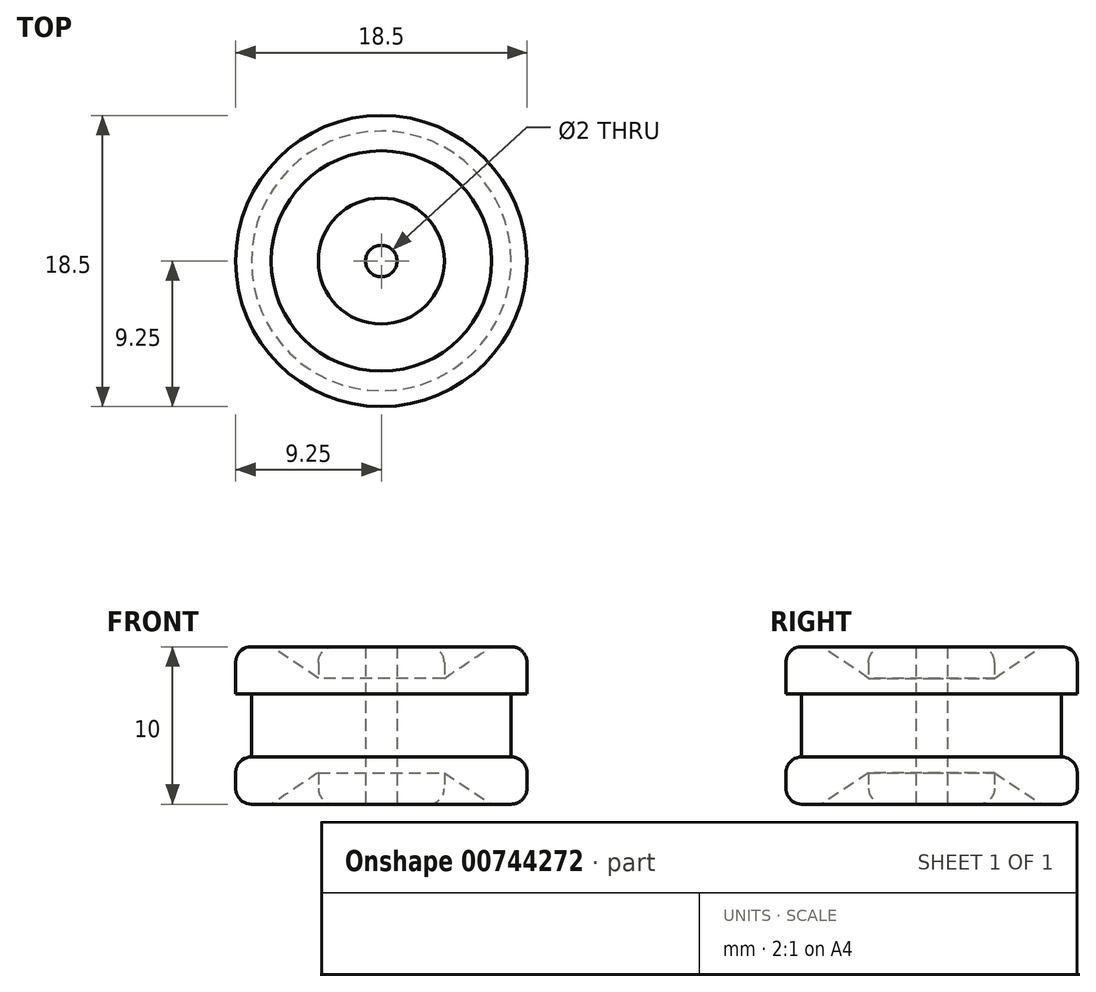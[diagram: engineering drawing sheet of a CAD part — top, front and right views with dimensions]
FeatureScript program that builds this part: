
annotation { "Feature Type Name" : "Feature", "Feature Type Description" : "" }
export const myFeature = defineFeature(function(context is Context, id is Id, definition is map)
    precondition{}
    {
        {
            var Q0;
            Q0=qCreatedBy(makeId("Top.planeOp"),FACE);
            var sketch = newSketch(context, id + "F0", { "sketchPlane" : qUnion([Q0])});
            skCircle(sketch, "E0", {"center": v(0, 0) * mm, "radius": 9.25 * mm});
            skCircle(sketch, "E1", {"center": v(0, 0) * mm, "radius": 1 * mm});
            skSolve(sketch);
        }
        {
            var Q0;
            Q0 = qSketchRegion(id + "F0", true);
            extrude(context, id + "F1", {"entities" : qUnion([Q0]), "depth" : 10 * mm, "offsetDistance" : 25 * mm});
        }
        {
            var Q0;
            Q0=makeQuery(id+"F1.opExtrude","CAP_FACE",FACE,{"disambiguationData":[OSD([sQuery(id+"F0.wireOp",EDGE,"E0"),sQuery(id+"F0.wireOp",EDGE,"E1")])],"isStart":false});
            cPlane(context, id + "F2", {"entities" : qUnion([Q0]), "cplaneType" : CPlaneType.OFFSET, "offset" : 2 * mm, "oppositeDirection" : true, "width" : 150 * mm, "height" : 150 * mm});
        }
        {
            var Q0;
            Q0=qCreatedBy(id+"F2.planeOp",FACE);
            var sketch = newSketch(context, id + "F3", { "sketchPlane" : qUnion([Q0])});
            skCircle(sketch, "E2", {"center": v(0, 0) * mm, "radius": 4 * mm});
            skSolve(sketch);
        }
        {
            var Q0;
            Q0=makeQuery(id+"F1.opExtrude","CAP_FACE",FACE,{"disambiguationData":[OSD([sQuery(id+"F0.wireOp",EDGE,"E0"),sQuery(id+"F0.wireOp",EDGE,"E1")])],"isStart":false});
            var sketch = newSketch(context, id + "F4", { "sketchPlane" : qUnion([Q0])});
            skCircle(sketch, "E3", {"center": v(0, 0) * mm, "radius": 7 * mm});
            skSolve(sketch);
        }
        {
            var Q1;
            Q1 = qSketchRegion(id + "F4", true);
            var Q2;
            Q2 = qSketchRegion(id + "F3", true);
            loft(context, id + "F5", {"operationType" : NewBodyOperationType.REMOVE, "sheetProfilesArray" : [{ "sheetProfileEntities" : qUnion([Q1]) }, { "sheetProfileEntities" : qUnion([Q2]) }]});
        }
        {
            var Q0;
            Q0=makeQuery(id+"F0.imprint","IMPRINT",FACE,{"disambiguationData":[TD([[makeQuery(id+"F0.imprint","IMPRINT",EDGE,{"derivedFrom":sQuery(id+"F0.wireOp",EDGE,"E0")}),1.0]])]});
            cPlane(context, id + "F6", {"entities" : qUnion([Q0]), "cplaneType" : CPlaneType.OFFSET, "offset" : 2 * mm, "width" : 150 * mm, "height" : 150 * mm});
        }
        {
            var Q0;
            Q0=qCreatedBy(id+"F6.planeOp",FACE);
            var sketch = newSketch(context, id + "F7", { "sketchPlane" : qUnion([Q0])});
            skCircle(sketch, "E4", {"center": v(0, 0) * mm, "radius": 4 * mm});
            skSolve(sketch);
        }
        {
            var Q0;
            Q0=makeQuery(id+"F0.imprint","IMPRINT",FACE,{"disambiguationData":[TD([[makeQuery(id+"F0.imprint","IMPRINT",EDGE,{"derivedFrom":sQuery(id+"F0.wireOp",EDGE,"E0")}),1.0]])]});
            var sketch = newSketch(context, id + "F8", { "sketchPlane" : qUnion([Q0])});
            skCircle(sketch, "E5", {"center": v(0, 0) * mm, "radius": 7 * mm});
            skSolve(sketch);
        }
        {
            var Q1;
            Q1 = qSketchRegion(id + "F8", true);
            var Q2;
            Q2 = qSketchRegion(id + "F7", true);
            loft(context, id + "F9", {"operationType" : NewBodyOperationType.REMOVE, "sheetProfilesArray" : [{ "sheetProfileEntities" : qUnion([Q1]) }, { "sheetProfileEntities" : qUnion([Q2]) }]});
        }
        {
            var Q0;
            Q0=makeQuery(id+"F5.boolean.opBoolean","COPY",FACE,{"derivedFrom":makeQuery(id+"F5.opLoft","CAP_FACE",FACE,{"disambiguationData":[OSD([makeQuery(id+"F3.imprint","IMPRINT",FACE,{"disambiguationData":[TD([[makeQuery(id+"F3.imprint","IMPRINT",EDGE,{"derivedFrom":sQuery(id+"F3.wireOp",EDGE,"E2")}),1.0]])]})])],"isStart":true})});
            extrude(context, id + "F10", {"entities" : qUnion([Q0]), "operationType" : NewBodyOperationType.ADD, "depth" : 2 * mm, "offsetDistance" : 25 * mm});
        }
        {
            var Q0;
            Q0=makeQuery(id+"F0.imprint","IMPRINT",FACE,{"disambiguationData":[TD([[makeQuery(id+"F0.imprint","IMPRINT",EDGE,{"derivedFrom":sQuery(id+"F0.wireOp",EDGE,"E0")}),1.0]])]});
            var sketch = newSketch(context, id + "F11", { "sketchPlane" : qUnion([Q0])});
            skCircle(sketch, "E6", {"center": v(0, 0) * mm, "radius": 4 * mm});
            skCircle(sketch, "E7", {"center": v(0, 0) * mm, "radius": 1 * mm});
            skSolve(sketch);
        }
        {
            var Q0;
            Q0 = qSketchRegion(id + "F11", true);
            extrude(context, id + "F12", {"entities" : qUnion([Q0]), "operationType" : NewBodyOperationType.ADD, "endBound" : BoundingType.UP_TO_NEXT, "depth" : 25 * mm, "offsetDistance" : 25 * mm});
        }
        {
            var Q0;
            Q0=qCreatedBy(makeId("Top.planeOp"),FACE);
            cPlane(context, id + "F13", {"entities" : qUnion([Q0]), "cplaneType" : CPlaneType.OFFSET, "offset" : 3 * mm, "width" : 150 * mm, "height" : 150 * mm});
        }
        {
            var Q0;
            Q0=qCreatedBy(id+"F13.planeOp",FACE);
            var sketch = newSketch(context, id + "F14", { "sketchPlane" : qUnion([Q0])});
            skCircle(sketch, "E8", {"center": v(0, 0) * mm, "radius": 9.25 * mm});
            skCircle(sketch, "E9", {"center": v(0, 0) * mm, "radius": 8.25 * mm});
            skSolve(sketch);
        }
        {
            var Q0;
            Q0 = qSketchRegion(id + "F14", true);
            extrude(context, id + "F15", {"entities" : qUnion([Q0]), "operationType" : NewBodyOperationType.REMOVE, "depth" : 4 * mm, "offsetDistance" : 25 * mm});
        }
        {
            var Q0;
            Q0=makeQuery(id+"F10.opExtrude","CAP_EDGE",EDGE,{"disambiguationData":[OSD([sQuery(id+"F3.wireOp",EDGE,"E2")])],"isStart":false});
            var Q1;
            Q1=makeQuery(id+"F12.opExtrude","CAP_EDGE",EDGE,{"disambiguationData":[OSD([sQuery(id+"F11.wireOp",EDGE,"E6")])],"isStart":true});
            var Q2;
            Q2=makeQuery(id+"F1.opExtrude","CAP_EDGE",EDGE,{"disambiguationData":[OSD([sQuery(id+"F0.wireOp",EDGE,"E0")])],"isStart":false});
            var Q3;
            Q3=makeQuery(id+"F1.opExtrude","CAP_EDGE",EDGE,{"disambiguationData":[OSD([sQuery(id+"F0.wireOp",EDGE,"E0")])],"isStart":true});
            var Q4;
            Q4=makeQuery(id+"F15.boolean.opBoolean","COPY",EDGE,{"derivedFrom":makeQuery(id+"F15.opExtrude","CAP_EDGE",EDGE,{"disambiguationData":[OSD([sQuery(id+"F14.wireOp",EDGE,"E8")])],"isStart":false})});
            var Q5;
            Q5=makeQuery(id+"F15.boolean.opBoolean","COPY",EDGE,{"derivedFrom":makeQuery(id+"F15.opExtrude","CAP_EDGE",EDGE,{"disambiguationData":[OSD([sQuery(id+"F14.wireOp",EDGE,"E8")])],"isStart":true})});
            fillet(context, id + "F16", {"entities" : qUnion([Q0, Q1, Q2, Q3, Q4, Q5]), "radius" : 1 * mm, "tangentPropagation" : true, "allowEdgeOverflow" : false});
        }
    });
